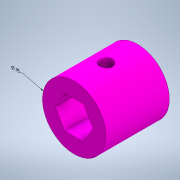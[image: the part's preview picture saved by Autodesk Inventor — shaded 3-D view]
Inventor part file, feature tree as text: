
AUTODESK INVENTOR PART (.ipt)
format: ipt  version: 2022.1 (Build 261234000, 234)  size: 139,776 bytes
history: native  units: in
note: dims shown in document units (in); Inventor stores cm internally (conversion verified against a paired STEP export)
features: other x3, sketch x2, extrude x1, plane x1, hole x1
ambient origin geometry x8: Origin, YZ Plane, XZ Plane, XY Plane, X Axis, Y Axis, Z Axis, Center Point
bodies: Solid1 (feature_tree)
feature tree (8):
  other  "Annotations"
  extrude  "Extrusion1"  Depth=0.75in
  other  "Thicken Hex"
  plane  "Work Plane1"
  hole  "Hole1"  [1 undecoded]
  sketch  "Sketch1"  dims[d0=0.375in d2=0.75in]
  sketch  "Sketch3"  dims[d3=0.1585in d4=0.75in d5=0.0in d6=0.005in d7=0.005in d10=0.15in d11=0.75in d12=0.5in d13=0.093in d14=0.5635in d15=0.25in d16=0.8108in d8=1.1428in d9=0.75in]
  other  "Diameter Dimension 1"
note: 1 required parameter value undecoded (feature->parameter linkage not recoverable at this tier; creation-order binding heuristic only, values carry confidence <= 0.55)
